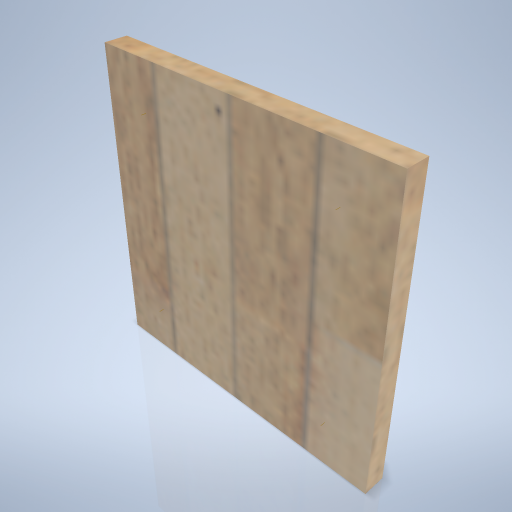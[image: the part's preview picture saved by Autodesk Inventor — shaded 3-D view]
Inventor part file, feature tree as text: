
AUTODESK INVENTOR PART (.ipt)
format: ipt  version: 2024.2 (Build 282272000, 272)  size: 377,856 bytes
history: native  units: mm
features: other x8, sketch x3, hole x2, extrude x1, chamfer x1
ambient origin geometry x8: Origin, YZ Plane, XZ Plane, XY Plane, X Axis, Y Axis, Z Axis, Center Point
bodies: Volumenkörper1 (feature_tree)
feature tree (15):
  extrude  "Extrusion1"  Depth=200.0mm
  chamfer  "Fasen1"  Distance=25.0mm
  hole  "Bohrung1"  [1 undecoded]
  hole  "Bohrung2"  [1 undecoded]
  other  "Arbeitsachse9"
  other  "Arbeitsachse10"
  other  "Arbeitsachse11"
  other  "Arbeitspunkt9"
  other  "Arbeitspunkt10"
  other  "Arbeitspunkt11"
  other  "Arbeitspunkt12"
  sketch  "Skizze1"  dims[d0=200.0mm d1=200.0mm d2=25.0mm d3=0.0mm]
  sketch  "Skizze2"  dims[d4=10.0mm d5=2.0mm d6=45.0deg]
  sketch  "Skizze3"  dims[d7=53.0mm d8=8.0mm d9=4.0mm d10=2.0mm d11=90.0deg d12=3.0mm d13=0.0mm d14=8.0mm d15=6.0mm d16=4.0mm d17=2.0mm d18=90.0deg d19=3.0mm d20=0.0mm d21=68.5mm d22=68.5mm d23=137.0mm d24=68.5mm d25=68.5mm]
  other  "Arbeitsachse12"
note: 2 required parameter values undecoded (feature->parameter linkage not recoverable at this tier; creation-order binding heuristic only, values carry confidence <= 0.55)
